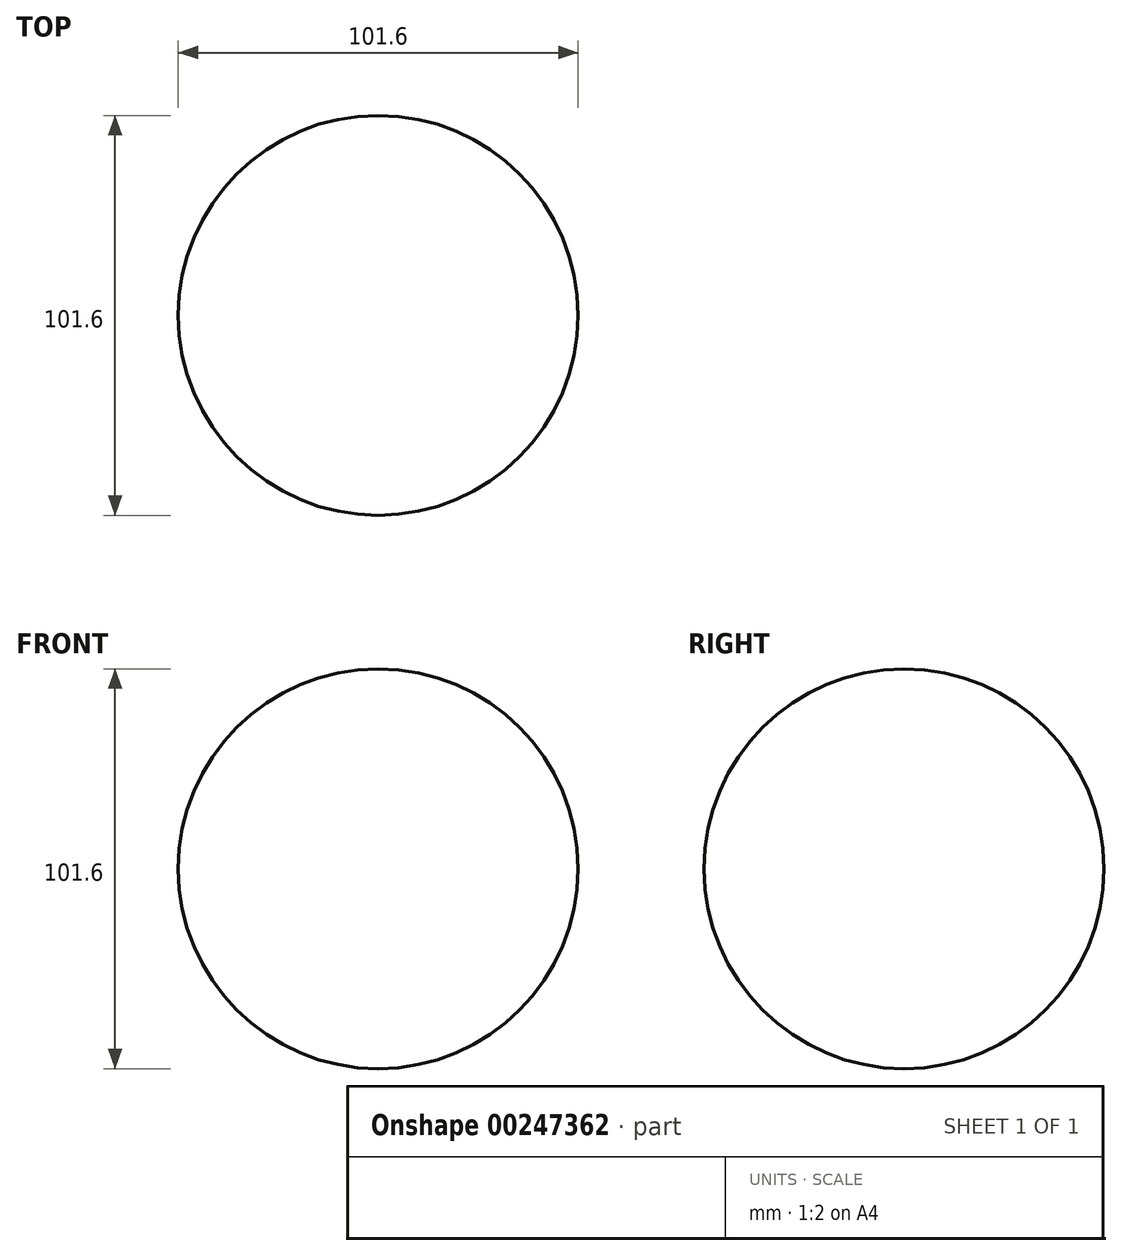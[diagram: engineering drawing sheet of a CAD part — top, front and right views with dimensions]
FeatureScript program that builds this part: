
annotation { "Feature Type Name" : "Feature", "Feature Type Description" : "" }
export const myFeature = defineFeature(function(context is Context, id is Id, definition is map)
    precondition{}
    {
        {
            var Q0;
            Q0=qCreatedBy(makeId("Front.planeOp"),FACE);
            var sketch = newSketch(context, id + "F0", { "sketchPlane" : qUnion([Q0])});
            skArc(sketch, "E0", {"start": v(-50.8, 0) * mm, "mid": v(0, -50.8) * mm, "end": v(50.8, 0) * mm});
            skLineSegment(sketch, "E1", {"start": v(-50.8, 0) * mm, "end": v(50.8, 0) * mm});
            skSolve(sketch);
        }
        {
            var Q0;
            Q0 = qSketchRegion(id + "F0", true);
            var Q1;
            Q1=sQuery(id+"F0.wireOp",EDGE,"E1");
            revolve(context, id + "F1", {"entities" : qUnion([Q0]), "axis" : qUnion([Q1]), "revolveType" : RevolveType.FULL});
        }
    });
